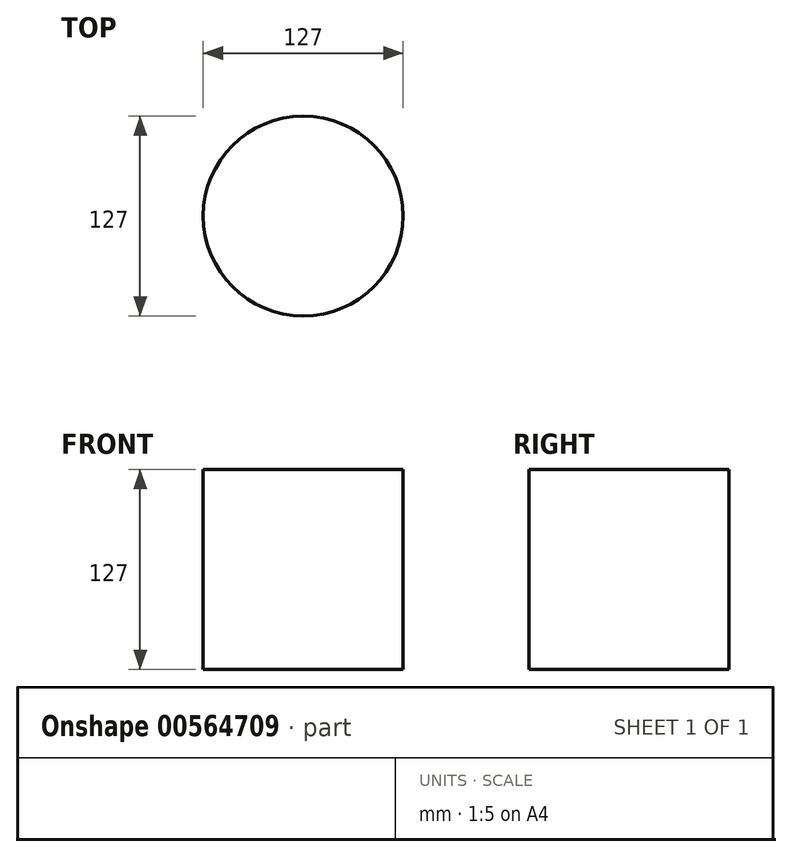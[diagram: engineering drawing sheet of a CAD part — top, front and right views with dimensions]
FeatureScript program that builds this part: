
annotation { "Feature Type Name" : "Feature", "Feature Type Description" : "" }
export const myFeature = defineFeature(function(context is Context, id is Id, definition is map)
    precondition{}
    {
        {
            var Q0;
            Q0=qCreatedBy(makeId("Top.planeOp"),FACE);
            var sketch = newSketch(context, id + "F0", { "sketchPlane" : qUnion([Q0])});
            skCircle(sketch, "E0", {"center": v(0, 0) * mm, "radius": 63.5 * mm});
            skSolve(sketch);
        }
        {
            var Q0;
            Q0=makeQuery(id+"F0.imprint","IMPRINT",FACE,{"disambiguationData":[TD([[makeQuery(id+"F0.imprint","IMPRINT",EDGE,{"derivedFrom":sQuery(id+"F0.wireOp",EDGE,"E0")}),1.0]])]});
            var Q1;
            Q1=sQuery(id+"F0.wireOp",EDGE,"E0");
            extrude(context, id + "F1", {"entities" : qUnion([Q0]), "surfaceEntities" : qUnion([Q1]), "depth" : 127 * mm, "offsetDistance" : 25.4 * mm});
        }
    });
